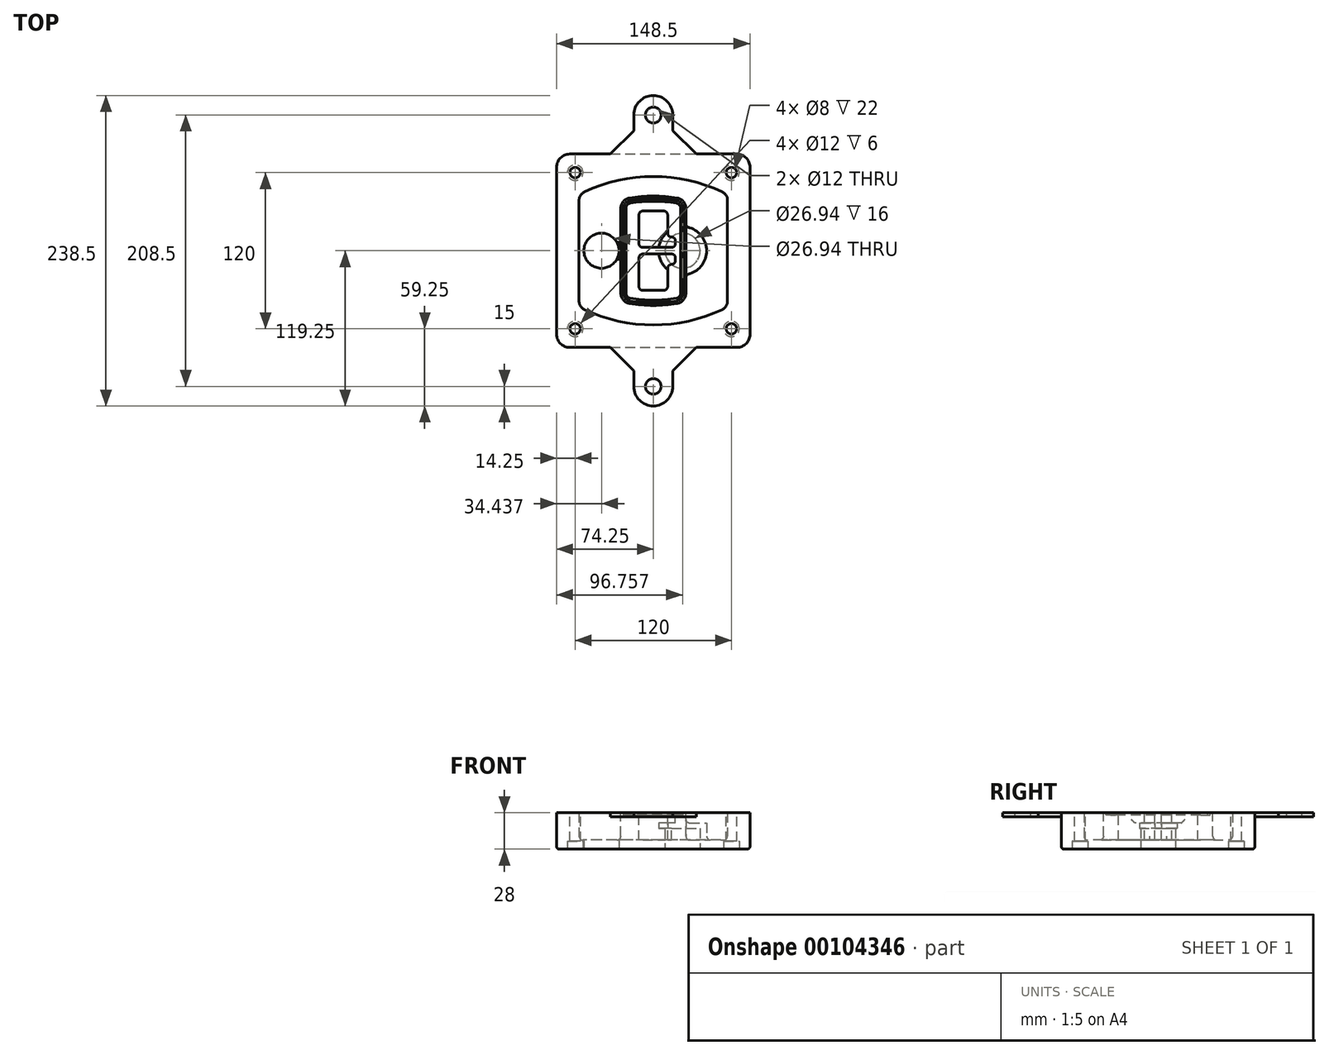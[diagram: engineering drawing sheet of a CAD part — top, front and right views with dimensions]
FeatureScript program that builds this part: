
annotation { "Feature Type Name" : "Feature", "Feature Type Description" : "" }
export const myFeature = defineFeature(function(context is Context, id is Id, definition is map)
    precondition{}
    {
        {
            var Q0;
            Q0=qCreatedBy(makeId("Top.planeOp"),FACE);
            var sketch = newSketch(context, id + "F0", { "sketchPlane" : qUnion([Q0])});
            skPoint(sketch, "E0.rect.middle", {"position": v(0, 0) * mm});
            skLineSegment(sketch, "E1.bottom", {"start": v(-64.25, -74.25) * mm, "end": v(64.25, -74.25) * mm});
            skLineSegment(sketch, "E1.top", {"start": v(-64.25, 74.25) * mm, "end": v(64.25, 74.25) * mm});
            skLineSegment(sketch, "E1.left", {"start": v(-74.25, -64.25) * mm, "end": v(-74.25, 64.25) * mm});
            skLineSegment(sketch, "E1.right", {"start": v(74.25, -64.25) * mm, "end": v(74.25, 64.25) * mm});
            skLineSegment(sketch, "E2", {"start": v(-74.25, 74.25) * mm, "end": v(74.25, -74.25) * mm, "construction": true});
            skLineSegment(sketch, "E3", {"start": v(74.25, 74.25) * mm, "end": v(-74.25, -74.25) * mm, "construction": true});
            skCircle(sketch, "E4", {"center": v(-60, 60) * mm, "radius": 4 * mm});
            skCircle(sketch, "E5", {"center": v(60, 60) * mm, "radius": 4 * mm});
            skCircle(sketch, "E6", {"center": v(60, -60) * mm, "radius": 4 * mm});
            skCircle(sketch, "E7", {"center": v(-60, -60) * mm, "radius": 4 * mm});
            skLineSegment(sketch, "E8", {"start": v(-60, 60) * mm, "end": v(60, 60) * mm, "construction": true});
            skLineSegment(sketch, "E9", {"start": v(60, 60) * mm, "end": v(60, -60) * mm, "construction": true});
            skLineSegment(sketch, "E10", {"start": v(60, -60) * mm, "end": v(-60, -60) * mm, "construction": true});
            skLineSegment(sketch, "E11", {"start": v(-60, -60) * mm, "end": v(-60, 60) * mm, "construction": true});
            skLineSegment(sketch, "E12", {"start": v(-60, 38.83) * mm, "end": v(-60, -38.83) * mm});
            skLineSegment(sketch, "E13", {"start": v(60, 38.83) * mm, "end": v(60, -38.83) * mm});
            skArc(sketch, "E14", {"start": v(54.26, 47.88) * mm, "mid": v(0, 60) * mm, "end": v(-54.26, 47.88) * mm});
            skArc(sketch, "E15", {"start": v(-54.26, -47.88) * mm, "mid": v(0, -60) * mm, "end": v(54.26, -47.88) * mm});
            skLineSegment(sketch, "E16", {"start": v(-60, 0) * mm, "end": v(60, 0) * mm, "construction": true});
            skPoint(sketch, "E17.visualSharp", {"position": v(-60, -45) * mm});
            skArc(sketch, "E17.filletArc", {"start": v(-60, -38.83) * mm, "mid": v(-58.44, -44.2) * mm, "end": v(-54.26, -47.88) * mm});
            skPoint(sketch, "E18.visualSharp", {"position": v(-60, 45) * mm});
            skArc(sketch, "E18.filletArc", {"start": v(-54.26, 47.88) * mm, "mid": v(-58.44, 44.2) * mm, "end": v(-60, 38.83) * mm});
            skPoint(sketch, "E19.visualSharp", {"position": v(60, 45) * mm});
            skArc(sketch, "E19.filletArc", {"start": v(60, 38.83) * mm, "mid": v(58.44, 44.2) * mm, "end": v(54.26, 47.88) * mm});
            skPoint(sketch, "E20.visualSharp", {"position": v(60, -45) * mm});
            skArc(sketch, "E20.filletArc", {"start": v(54.26, -47.88) * mm, "mid": v(58.44, -44.2) * mm, "end": v(60, -38.83) * mm});
            skPoint(sketch, "E21.visualSharp", {"position": v(-74.25, 74.25) * mm});
            skArc(sketch, "E21.filletArc", {"start": v(-64.25, 74.25) * mm, "mid": v(-71.32, 71.32) * mm, "end": v(-74.25, 64.25) * mm});
            skPoint(sketch, "E22.visualSharp", {"position": v(74.25, 74.25) * mm});
            skArc(sketch, "E22.filletArc", {"start": v(74.25, 64.25) * mm, "mid": v(71.32, 71.32) * mm, "end": v(64.25, 74.25) * mm});
            skPoint(sketch, "E23.visualSharp", {"position": v(74.25, -74.25) * mm});
            skArc(sketch, "E23.filletArc", {"start": v(64.25, -74.25) * mm, "mid": v(71.32, -71.32) * mm, "end": v(74.25, -64.25) * mm});
            skPoint(sketch, "E24.visualSharp", {"position": v(-74.25, -74.25) * mm});
            skArc(sketch, "E24.filletArc", {"start": v(-74.25, -64.25) * mm, "mid": v(-71.32, -71.32) * mm, "end": v(-64.25, -74.25) * mm});
            skArc(sketch, "E25.0", {"start": v(57, 38.83) * mm, "mid": v(55.9, 42.58) * mm, "end": v(52.98, 45.17) * mm});
            skLineSegment(sketch, "E25.1", {"start": v(57, 38.83) * mm, "end": v(57, -38.83) * mm});
            skArc(sketch, "E25.2", {"start": v(52.98, -45.17) * mm, "mid": v(55.9, -42.58) * mm, "end": v(57, -38.83) * mm});
            skArc(sketch, "E25.3", {"start": v(-52.98, -45.17) * mm, "mid": v(0, -57) * mm, "end": v(52.98, -45.17) * mm});
            skArc(sketch, "E25.4", {"start": v(-57, -38.83) * mm, "mid": v(-55.9, -42.58) * mm, "end": v(-52.98, -45.17) * mm});
            skArc(sketch, "E25.5", {"start": v(52.98, 45.17) * mm, "mid": v(0, 57) * mm, "end": v(-52.98, 45.17) * mm});
            skLineSegment(sketch, "E25.6", {"start": v(-57, 38.83) * mm, "end": v(-57, -38.83) * mm});
            skArc(sketch, "E25.7", {"start": v(-52.98, 45.17) * mm, "mid": v(-55.9, 42.58) * mm, "end": v(-57, 38.83) * mm});
            skArc(sketch, "E26.0", {"start": v(-55.96, 51.5) * mm, "mid": v(-61.82, 46.33) * mm, "end": v(-64, 38.83) * mm});
            skArc(sketch, "E26.1", {"start": v(55.96, 51.5) * mm, "mid": v(0, 64) * mm, "end": v(-55.96, 51.5) * mm});
            skArc(sketch, "E26.2", {"start": v(64, 38.83) * mm, "mid": v(61.82, 46.33) * mm, "end": v(55.96, 51.5) * mm});
            skLineSegment(sketch, "E26.3", {"start": v(64, 38.83) * mm, "end": v(64, -38.83) * mm});
            skArc(sketch, "E26.4", {"start": v(55.96, -51.5) * mm, "mid": v(61.82, -46.33) * mm, "end": v(64, -38.83) * mm});
            skLineSegment(sketch, "E26.5", {"start": v(-64, 38.83) * mm, "end": v(-64, -38.83) * mm});
            skArc(sketch, "E26.6", {"start": v(-55.96, -51.5) * mm, "mid": v(0, -64) * mm, "end": v(55.96, -51.5) * mm});
            skArc(sketch, "E26.7", {"start": v(-64, -38.83) * mm, "mid": v(-61.82, -46.33) * mm, "end": v(-55.96, -51.5) * mm});
            skSolve(sketch);
        }
        {
            var Q0;
            Q0=makeQuery(id+"F0.imprint","IMPRINT",FACE,{"disambiguationData":[TD([[makeQuery(id+"F0.imprint","IMPRINT",EDGE,{"derivedFrom":sQuery(id+"F0.wireOp",EDGE,"E1.bottom")}),1.0]])]});
            var Q1;
            Q1=makeQuery(id+"F0.imprint","IMPRINT",FACE,{"disambiguationData":[TD([[makeQuery(id+"F0.imprint","IMPRINT",EDGE,{"derivedFrom":sQuery(id+"F0.wireOp",EDGE,"E12")}),1.0]])]});
            var Q2;
            Q2=makeQuery(id+"F0.imprint","IMPRINT",FACE,{"disambiguationData":[TD([[makeQuery(id+"F0.imprint","IMPRINT",EDGE,{"derivedFrom":sQuery(id+"F0.wireOp",EDGE,"E25.0")}),1.0]])]});
            var Q3;
            Q3=makeQuery(id+"F0.imprint","IMPRINT",FACE,{"disambiguationData":[TD([[makeQuery(id+"F0.imprint","IMPRINT",EDGE,{"derivedFrom":sQuery(id+"F0.wireOp",EDGE,"E12")}),-1.0]])]});
            extrude(context, id + "F1", {"entities" : qUnion([Q0, Q1, Q2, Q3]), "oppositeDirection" : true, "depth" : 25 * mm});
        }
        {
            var Q0;
            Q0=makeQuery(id+"F0.imprint","IMPRINT",FACE,{"disambiguationData":[TD([[makeQuery(id+"F0.imprint","IMPRINT",EDGE,{"derivedFrom":sQuery(id+"F0.wireOp",EDGE,"E12")}),1.0]])]});
            extrude(context, id + "F2", {"entities" : qUnion([Q0]), "operationType" : NewBodyOperationType.ADD, "depth" : 3 * mm});
        }
        {
            var Q0;
            Q0=makeQuery(id+"F0.imprint","IMPRINT",FACE,{"disambiguationData":[TD([[makeQuery(id+"F0.imprint","IMPRINT",EDGE,{"derivedFrom":sQuery(id+"F0.wireOp",EDGE,"E25.0")}),1.0]])]});
            extrude(context, id + "F3", {"entities" : qUnion([Q0]), "operationType" : NewBodyOperationType.REMOVE, "oppositeDirection" : true, "depth" : 18 * mm});
        }
        {
            var Q0;
            Q0=makeQuery(id+"F2.opExtrude","CAP_FACE",FACE,{"disambiguationData":[OSD([sQuery(id+"F0.wireOp",EDGE,"E12"),sQuery(id+"F0.wireOp",EDGE,"E13"),sQuery(id+"F0.wireOp",EDGE,"E14"),sQuery(id+"F0.wireOp",EDGE,"E15"),sQuery(id+"F0.wireOp",EDGE,"E17.filletArc"),sQuery(id+"F0.wireOp",EDGE,"E18.filletArc"),sQuery(id+"F0.wireOp",EDGE,"E19.filletArc"),sQuery(id+"F0.wireOp",EDGE,"E20.filletArc"),sQuery(id+"F0.wireOp",EDGE,"E25.0"),sQuery(id+"F0.wireOp",EDGE,"E25.1"),sQuery(id+"F0.wireOp",EDGE,"E25.2"),sQuery(id+"F0.wireOp",EDGE,"E25.3"),sQuery(id+"F0.wireOp",EDGE,"E25.4"),sQuery(id+"F0.wireOp",EDGE,"E25.5"),sQuery(id+"F0.wireOp",EDGE,"E25.6"),sQuery(id+"F0.wireOp",EDGE,"E25.7")])],"isStart":false});
            var sketch = newSketch(context, id + "F4", { "sketchPlane" : qUnion([Q0])});
            skArc(sketch, "E27.0", {"start": v(-18.34, -40.45) * mm, "mid": v(0, -42) * mm, "end": v(18.34, -40.45) * mm});
            skArc(sketch, "E28.0", {"start": v(18.34, 40.45) * mm, "mid": v(0, 42) * mm, "end": v(-18.34, 40.45) * mm});
            skLineSegment(sketch, "E29", {"start": v(-25, 32.57) * mm, "end": v(-25, -32.57) * mm});
            skLineSegment(sketch, "E30", {"start": v(25, 32.57) * mm, "end": v(25, -32.57) * mm});
            skLineSegment(sketch, "E31", {"start": v(-25, 39.1) * mm, "end": v(25, 39.1) * mm, "construction": true});
            skLineSegment(sketch, "E32", {"start": v(-25, -39.1) * mm, "end": v(25, -39.1) * mm, "construction": true});
            skPoint(sketch, "E33.visualSharp", {"position": v(-25, 39.1) * mm});
            skArc(sketch, "E33.filletArc", {"start": v(-18.34, 40.45) * mm, "mid": v(-23.11, 37.73) * mm, "end": v(-25, 32.57) * mm});
            skPoint(sketch, "E34.visualSharp", {"position": v(25, 39.1) * mm});
            skArc(sketch, "E34.filletArc", {"start": v(25, 32.57) * mm, "mid": v(23.11, 37.73) * mm, "end": v(18.34, 40.45) * mm});
            skPoint(sketch, "E35.visualSharp", {"position": v(25, -39.1) * mm});
            skArc(sketch, "E35.filletArc", {"start": v(18.34, -40.45) * mm, "mid": v(23.11, -37.73) * mm, "end": v(25, -32.57) * mm});
            skPoint(sketch, "E36.visualSharp", {"position": v(-25, -39.1) * mm});
            skArc(sketch, "E36.filletArc", {"start": v(-25, -32.57) * mm, "mid": v(-23.11, -37.73) * mm, "end": v(-18.34, -40.45) * mm});
            skArc(sketch, "E37.0", {"start": v(52.98, 45.17) * mm, "mid": v(0, 57) * mm, "end": v(-52.98, 45.17) * mm});
            skArc(sketch, "E37.1", {"start": v(-52.98, 45.17) * mm, "mid": v(-55.9, 42.58) * mm, "end": v(-57, 38.83) * mm});
            skLineSegment(sketch, "E37.2", {"start": v(-57, 38.83) * mm, "end": v(-57, -38.83) * mm});
            skArc(sketch, "E37.3", {"start": v(-57, -38.83) * mm, "mid": v(-55.9, -42.58) * mm, "end": v(-52.98, -45.17) * mm});
            skArc(sketch, "E37.4", {"start": v(-52.98, -45.17) * mm, "mid": v(0, -57) * mm, "end": v(52.98, -45.17) * mm});
            skArc(sketch, "E37.5", {"start": v(52.98, -45.17) * mm, "mid": v(55.9, -42.58) * mm, "end": v(57, -38.83) * mm});
            skLineSegment(sketch, "E37.6", {"start": v(57, 38.83) * mm, "end": v(57, -38.83) * mm});
            skArc(sketch, "E37.7", {"start": v(57, 38.83) * mm, "mid": v(55.9, 42.58) * mm, "end": v(52.98, 45.17) * mm});
            skLineSegment(sketch, "E38.0", {"start": v(23, 32.57) * mm, "end": v(23, -32.57) * mm});
            skArc(sketch, "E38.1", {"start": v(18, -38.48) * mm, "mid": v(21.58, -36.44) * mm, "end": v(23, -32.57) * mm});
            skArc(sketch, "E38.2", {"start": v(-18, -38.48) * mm, "mid": v(0, -40) * mm, "end": v(18, -38.48) * mm});
            skArc(sketch, "E38.3", {"start": v(-23, -32.57) * mm, "mid": v(-21.58, -36.44) * mm, "end": v(-18, -38.48) * mm});
            skLineSegment(sketch, "E38.4", {"start": v(-23, 32.57) * mm, "end": v(-23, -32.57) * mm});
            skArc(sketch, "E38.5", {"start": v(23, 32.57) * mm, "mid": v(21.58, 36.44) * mm, "end": v(18, 38.48) * mm});
            skArc(sketch, "E38.6", {"start": v(-18, 38.48) * mm, "mid": v(-21.58, 36.44) * mm, "end": v(-23, 32.57) * mm});
            skArc(sketch, "E38.7", {"start": v(18, 38.48) * mm, "mid": v(0, 40) * mm, "end": v(-18, 38.48) * mm});
            skArc(sketch, "E39.0", {"start": v(21, 32.57) * mm, "mid": v(20.06, 35.15) * mm, "end": v(17.67, 36.5) * mm});
            skLineSegment(sketch, "E39.1", {"start": v(21, 32.57) * mm, "end": v(21, -32.57) * mm});
            skArc(sketch, "E39.2", {"start": v(17.67, -36.5) * mm, "mid": v(20.06, -35.15) * mm, "end": v(21, -32.57) * mm});
            skArc(sketch, "E39.3", {"start": v(-17.67, -36.5) * mm, "mid": v(0, -38) * mm, "end": v(17.67, -36.5) * mm});
            skArc(sketch, "E39.4", {"start": v(-21, -32.57) * mm, "mid": v(-20.06, -35.15) * mm, "end": v(-17.67, -36.5) * mm});
            skArc(sketch, "E39.5", {"start": v(17.67, 36.5) * mm, "mid": v(0, 38) * mm, "end": v(-17.67, 36.5) * mm});
            skLineSegment(sketch, "E39.6", {"start": v(-21, 32.57) * mm, "end": v(-21, -32.57) * mm});
            skArc(sketch, "E39.7", {"start": v(-17.67, 36.5) * mm, "mid": v(-20.06, 35.15) * mm, "end": v(-21, 32.57) * mm});
            skLineSegment(sketch, "E40", {"start": v(-25, 0) * mm, "end": v(25, 0) * mm, "construction": true});
            skLineSegment(sketch, "E41", {"start": v(-11, 5.5) * mm, "end": v(-11, 27.5) * mm});
            skLineSegment(sketch, "E42", {"start": v(-8, 30.5) * mm, "end": v(8, 30.5) * mm});
            skLineSegment(sketch, "E43", {"start": v(11, 27.5) * mm, "end": v(11, 13.5) * mm});
            skLineSegment(sketch, "E44", {"start": v(14, 10.5) * mm, "end": v(14, 10.5) * mm});
            skLineSegment(sketch, "E45", {"start": v(17, 7.5) * mm, "end": v(17, 5.5) * mm});
            skLineSegment(sketch, "E46", {"start": v(14, 2.5) * mm, "end": v(-8, 2.5) * mm});
            skPoint(sketch, "E47.visualSharp", {"position": v(-11, 30.5) * mm});
            skArc(sketch, "E47.filletArc", {"start": v(-8, 30.5) * mm, "mid": v(-10.12, 29.62) * mm, "end": v(-11, 27.5) * mm});
            skPoint(sketch, "E48.visualSharp", {"position": v(11, 30.5) * mm});
            skArc(sketch, "E48.filletArc", {"start": v(11, 27.5) * mm, "mid": v(10.12, 29.62) * mm, "end": v(8, 30.5) * mm});
            skPoint(sketch, "E49.visualSharp", {"position": v(11, 10.5) * mm});
            skArc(sketch, "E49.filletArc", {"start": v(11, 13.5) * mm, "mid": v(11.88, 11.38) * mm, "end": v(14, 10.5) * mm});
            skPoint(sketch, "E50.visualSharp", {"position": v(17, 10.5) * mm});
            skArc(sketch, "E50.filletArc", {"start": v(17, 7.5) * mm, "mid": v(16.12, 9.62) * mm, "end": v(14, 10.5) * mm});
            skPoint(sketch, "E51.visualSharp", {"position": v(17, 2.5) * mm});
            skArc(sketch, "E51.filletArc", {"start": v(14, 2.5) * mm, "mid": v(16.12, 3.38) * mm, "end": v(17, 5.5) * mm});
            skPoint(sketch, "E52.visualSharp", {"position": v(-11, 2.5) * mm});
            skArc(sketch, "E52.filletArc", {"start": v(-11, 5.5) * mm, "mid": v(-10.12, 3.38) * mm, "end": v(-8, 2.5) * mm});
            skLineSegment(sketch, "E53.0.MirrorCS", {"start": v(14, -2.5) * mm, "end": v(-8, -2.5) * mm});
            skArc(sketch, "E54.0.MirrorCS", {"start": v(-11, -5.5) * mm, "mid": v(-10.12, -3.38) * mm, "end": v(-8, -2.5) * mm});
            skLineSegment(sketch, "E55.0.MirrorCS", {"start": v(-11, -5.5) * mm, "end": v(-11, -27.5) * mm});
            skArc(sketch, "E56.0.MirrorCS", {"start": v(-8, -30.5) * mm, "mid": v(-10.12, -29.62) * mm, "end": v(-11, -27.5) * mm});
            skLineSegment(sketch, "E57.0.MirrorCS", {"start": v(-8, -30.5) * mm, "end": v(8, -30.5) * mm});
            skArc(sketch, "E58.0.MirrorCS", {"start": v(11, -27.5) * mm, "mid": v(10.12, -29.62) * mm, "end": v(8, -30.5) * mm});
            skLineSegment(sketch, "E59.0.MirrorCS", {"start": v(11, -27.5) * mm, "end": v(11, -13.5) * mm});
            skArc(sketch, "E60.0.MirrorCS", {"start": v(11, -13.5) * mm, "mid": v(11.88, -11.38) * mm, "end": v(14, -10.5) * mm});
            skArc(sketch, "E61.0.MirrorCS", {"start": v(17, -7.5) * mm, "mid": v(16.12, -9.62) * mm, "end": v(14, -10.5) * mm});
            skLineSegment(sketch, "E62.0.MirrorCS", {"start": v(17, -7.5) * mm, "end": v(17, -5.5) * mm});
            skArc(sketch, "E63.0.MirrorCS", {"start": v(14, -2.5) * mm, "mid": v(16.12, -3.38) * mm, "end": v(17, -5.5) * mm});
            skSolve(sketch);
        }
        {
            var Q0;
            Q0=makeQuery(id+"F4.imprint","IMPRINT",FACE,{"disambiguationData":[TD([[makeQuery(id+"F4.imprint","IMPRINT",EDGE,{"derivedFrom":sQuery(id+"F4.wireOp",EDGE,"E27.0")}),1.0]])]});
            var Q1;
            Q1=makeQuery(id+"F4.imprint","IMPRINT",FACE,{"disambiguationData":[TD([[makeQuery(id+"F4.imprint","IMPRINT",EDGE,{"derivedFrom":sQuery(id+"F4.wireOp",EDGE,"E38.0")}),-1.0]])]});
            var Q2;
            Q2=makeQuery(id+"F4.imprint","IMPRINT",FACE,{"disambiguationData":[TD([[makeQuery(id+"F4.imprint","IMPRINT",EDGE,{"derivedFrom":sQuery(id+"F4.wireOp",EDGE,"E39.0")}),1.0]])]});
            extrude(context, id + "F5", {"entities" : qUnion([Q0, Q1, Q2]), "operationType" : NewBodyOperationType.ADD, "endBound" : BoundingType.UP_TO_NEXT, "oppositeDirection" : true, "depth" : 25 * mm});
        }
        {
            var Q0;
            Q0=makeQuery(id+"F4.imprint","IMPRINT",FACE,{"disambiguationData":[TD([[makeQuery(id+"F4.imprint","IMPRINT",EDGE,{"derivedFrom":sQuery(id+"F4.wireOp",EDGE,"E38.0")}),-1.0]])]});
            extrude(context, id + "F6", {"entities" : qUnion([Q0]), "operationType" : NewBodyOperationType.REMOVE, "oppositeDirection" : true, "depth" : 2 * mm});
        }
        {
            var Q0;
            Q0=makeQuery(id+"F1.opExtrude","CAP_FACE",FACE,{"disambiguationData":[OSD([sQuery(id+"F0.wireOp",EDGE,"E1.bottom"),sQuery(id+"F0.wireOp",EDGE,"E1.top"),sQuery(id+"F0.wireOp",EDGE,"E1.left"),sQuery(id+"F0.wireOp",EDGE,"E1.right"),sQuery(id+"F0.wireOp",EDGE,"E4"),sQuery(id+"F0.wireOp",EDGE,"E5"),sQuery(id+"F0.wireOp",EDGE,"E6"),sQuery(id+"F0.wireOp",EDGE,"E7"),sQuery(id+"F0.wireOp",EDGE,"E21.filletArc"),sQuery(id+"F0.wireOp",EDGE,"E22.filletArc"),sQuery(id+"F0.wireOp",EDGE,"E23.filletArc"),sQuery(id+"F0.wireOp",EDGE,"E24.filletArc")])],"isStart":false});
            var sketch = newSketch(context, id + "F7", { "sketchPlane" : qUnion([Q0])});
            skCircle(sketch, "E64", {"center": v(22.5, 0) * mm, "radius": 13.47 * mm});
            skCircle(sketch, "E65", {"center": v(-39.81, 0) * mm, "radius": 13.47 * mm});
            skLineSegment(sketch, "E66", {"start": v(74.25, 0) * mm, "end": v(-74.25, 0) * mm});
            skCircle(sketch, "E67", {"center": v(22.5, 0) * mm, "radius": 18.47 * mm});
            skCircle(sketch, "E68", {"center": v(60, -60) * mm, "radius": 6 * mm});
            skCircle(sketch, "E69", {"center": v(-60, -60) * mm, "radius": 6 * mm});
            skCircle(sketch, "E70", {"center": v(-60, 60) * mm, "radius": 6 * mm});
            skCircle(sketch, "E71", {"center": v(60, 60) * mm, "radius": 6 * mm});
            skSolve(sketch);
        }
        {
            var Q0;
            {var subQ1=sQuery(id+"F7.wireOp",EDGE,"E66");var subQ4=sQuery(id+"F7.wireOp",EDGE,"E64");var subQ6=makeQuery(id+"F7.imprint","INTERSECT",VERTEX,{"disambiguationData":[OD(0.0)],"derivedFrom":[subQ4,subQ1]});Q0=makeQuery(id+"F7.imprint","IMPRINT",FACE,{"disambiguationData":[TD([[makeQuery(id+"F7.imprint","IMPRINT",EDGE,{"disambiguationData":[TD([[subQ6,-1.0]])],"derivedFrom":subQ4}),-1.0]])]});}
            var Q1;
            {var subQ0=sQuery(id+"F7.wireOp",EDGE,"E66");var subQ1=sQuery(id+"F7.wireOp",EDGE,"E64");var subQ3=makeQuery(id+"F7.imprint","INTERSECT",VERTEX,{"disambiguationData":[OD(0.0)],"derivedFrom":[subQ1,subQ0]});Q1=makeQuery(id+"F7.imprint","IMPRINT",FACE,{"disambiguationData":[TD([[makeQuery(id+"F7.imprint","IMPRINT",EDGE,{"disambiguationData":[TD([[subQ3,-1.0]])],"derivedFrom":subQ1}),1.0]])]});}
            var Q2;
            {var subQ0=sQuery(id+"F7.wireOp",EDGE,"E66");var subQ1=sQuery(id+"F7.wireOp",EDGE,"E64");var subQ3=makeQuery(id+"F7.imprint","INTERSECT",VERTEX,{"disambiguationData":[OD(0.0)],"derivedFrom":[subQ1,subQ0]});Q2=makeQuery(id+"F7.imprint","IMPRINT",FACE,{"disambiguationData":[TD([[makeQuery(id+"F7.imprint","IMPRINT",EDGE,{"disambiguationData":[TD([[subQ3,1.0]])],"derivedFrom":subQ1}),1.0]])]});}
            var Q3;
            {var subQ1=sQuery(id+"F7.wireOp",EDGE,"E66");var subQ4=sQuery(id+"F7.wireOp",EDGE,"E64");var subQ6=makeQuery(id+"F7.imprint","INTERSECT",VERTEX,{"disambiguationData":[OD(0.0)],"derivedFrom":[subQ4,subQ1]});Q3=makeQuery(id+"F7.imprint","IMPRINT",FACE,{"disambiguationData":[TD([[makeQuery(id+"F7.imprint","IMPRINT",EDGE,{"disambiguationData":[TD([[subQ6,1.0]])],"derivedFrom":subQ4}),-1.0]])]});}
            extrude(context, id + "F8", {"entities" : qUnion([Q0, Q1, Q2, Q3]), "operationType" : NewBodyOperationType.ADD, "oppositeDirection" : true, "depth" : 20 * mm});
        }
        {
            var Q0;
            {var subQ0=sQuery(id+"F7.wireOp",EDGE,"E66");var subQ1=sQuery(id+"F7.wireOp",EDGE,"E64");var subQ3=makeQuery(id+"F7.imprint","INTERSECT",VERTEX,{"disambiguationData":[OD(0.0)],"derivedFrom":[subQ1,subQ0]});Q0=makeQuery(id+"F7.imprint","IMPRINT",FACE,{"disambiguationData":[TD([[makeQuery(id+"F7.imprint","IMPRINT",EDGE,{"disambiguationData":[TD([[subQ3,-1.0]])],"derivedFrom":subQ1}),1.0]])]});}
            var Q1;
            {var subQ0=sQuery(id+"F7.wireOp",EDGE,"E66");var subQ1=sQuery(id+"F7.wireOp",EDGE,"E64");var subQ3=makeQuery(id+"F7.imprint","INTERSECT",VERTEX,{"disambiguationData":[OD(0.0)],"derivedFrom":[subQ1,subQ0]});Q1=makeQuery(id+"F7.imprint","IMPRINT",FACE,{"disambiguationData":[TD([[makeQuery(id+"F7.imprint","IMPRINT",EDGE,{"disambiguationData":[TD([[subQ3,1.0]])],"derivedFrom":subQ1}),1.0]])]});}
            extrude(context, id + "F9", {"entities" : qUnion([Q0, Q1]), "operationType" : NewBodyOperationType.REMOVE, "oppositeDirection" : true, "depth" : 16 * mm});
        }
        {
            var Q0;
            {var subQ0=sQuery(id+"F7.wireOp",EDGE,"E66");var subQ1=sQuery(id+"F7.wireOp",EDGE,"E65");var subQ3=makeQuery(id+"F7.imprint","INTERSECT",VERTEX,{"disambiguationData":[OD(0.0)],"derivedFrom":[subQ1,subQ0]});Q0=makeQuery(id+"F7.imprint","IMPRINT",FACE,{"disambiguationData":[TD([[makeQuery(id+"F7.imprint","IMPRINT",EDGE,{"disambiguationData":[TD([[subQ3,-1.0]])],"derivedFrom":subQ1}),1.0]])]});}
            var Q1;
            {var subQ0=sQuery(id+"F7.wireOp",EDGE,"E66");var subQ1=sQuery(id+"F7.wireOp",EDGE,"E65");var subQ3=makeQuery(id+"F7.imprint","INTERSECT",VERTEX,{"disambiguationData":[OD(0.0)],"derivedFrom":[subQ1,subQ0]});Q1=makeQuery(id+"F7.imprint","IMPRINT",FACE,{"disambiguationData":[TD([[makeQuery(id+"F7.imprint","IMPRINT",EDGE,{"disambiguationData":[TD([[subQ3,1.0]])],"derivedFrom":subQ1}),1.0]])]});}
            extrude(context, id + "F10", {"entities" : qUnion([Q0, Q1]), "operationType" : NewBodyOperationType.REMOVE, "oppositeDirection" : true, "depth" : 25 * mm});
        }
        {
            var Q0;
            Q0=makeQuery(id+"F7.imprint","IMPRINT",FACE,{"disambiguationData":[TD([[makeQuery(id+"F7.imprint","IMPRINT",EDGE,{"derivedFrom":sQuery(id+"F7.wireOp",EDGE,"E68")}),1.0]])]});
            var Q1;
            Q1=makeQuery(id+"F7.imprint","IMPRINT",FACE,{"disambiguationData":[TD([[makeQuery(id+"F7.imprint","IMPRINT",EDGE,{"derivedFrom":makeQuery(id+"F1.opExtrude","CAP_EDGE",EDGE,{"disambiguationData":[OSD([sQuery(id+"F0.wireOp",EDGE,"E5")])],"isStart":false})}),-1.0]])]});
            var Q2;
            Q2=makeQuery(id+"F7.imprint","IMPRINT",FACE,{"disambiguationData":[TD([[makeQuery(id+"F7.imprint","IMPRINT",EDGE,{"derivedFrom":sQuery(id+"F7.wireOp",EDGE,"E69")}),1.0]])]});
            var Q3;
            Q3=makeQuery(id+"F7.imprint","IMPRINT",FACE,{"disambiguationData":[TD([[makeQuery(id+"F7.imprint","IMPRINT",EDGE,{"derivedFrom":makeQuery(id+"F1.opExtrude","CAP_EDGE",EDGE,{"disambiguationData":[OSD([sQuery(id+"F0.wireOp",EDGE,"E4")])],"isStart":false})}),-1.0]])]});
            var Q4;
            Q4=makeQuery(id+"F7.imprint","IMPRINT",FACE,{"disambiguationData":[TD([[makeQuery(id+"F7.imprint","IMPRINT",EDGE,{"derivedFrom":sQuery(id+"F7.wireOp",EDGE,"E70")}),1.0]])]});
            var Q5;
            Q5=makeQuery(id+"F7.imprint","IMPRINT",FACE,{"disambiguationData":[TD([[makeQuery(id+"F7.imprint","IMPRINT",EDGE,{"derivedFrom":makeQuery(id+"F1.opExtrude","CAP_EDGE",EDGE,{"disambiguationData":[OSD([sQuery(id+"F0.wireOp",EDGE,"E7")])],"isStart":false})}),-1.0]])]});
            var Q6;
            Q6=makeQuery(id+"F7.imprint","IMPRINT",FACE,{"disambiguationData":[TD([[makeQuery(id+"F7.imprint","IMPRINT",EDGE,{"derivedFrom":sQuery(id+"F7.wireOp",EDGE,"E71")}),1.0]])]});
            var Q7;
            Q7=makeQuery(id+"F7.imprint","IMPRINT",FACE,{"disambiguationData":[TD([[makeQuery(id+"F7.imprint","IMPRINT",EDGE,{"derivedFrom":makeQuery(id+"F1.opExtrude","CAP_EDGE",EDGE,{"disambiguationData":[OSD([sQuery(id+"F0.wireOp",EDGE,"E6")])],"isStart":false})}),-1.0]])]});
            extrude(context, id + "F11", {"entities" : qUnion([Q0, Q1, Q2, Q3, Q4, Q5, Q6, Q7]), "operationType" : NewBodyOperationType.REMOVE, "oppositeDirection" : true, "depth" : 6 * mm});
        }
        {
            var Q0;
            Q0=makeQuery(id+"F9.boolean.opBoolean","COPY",FACE,{"derivedFrom":makeQuery(id+"F9.opExtrude","CAP_FACE",FACE,{"disambiguationData":[OSD([sQuery(id+"F7.wireOp",EDGE,"E64")])],"isStart":false})});
            var sketch = newSketch(context, id + "F12", { "sketchPlane" : qUnion([Q0])});
            skArc(sketch, "E72.0", {"start": v(11, 14.45) * mm, "mid": v(6.45, 9.13) * mm, "end": v(4.2, 2.5) * mm});
            skArc(sketch, "E72.1", {"start": v(4.2, -2.5) * mm, "mid": v(6.45, -9.13) * mm, "end": v(11, -14.45) * mm});
            skLineSegment(sketch, "E73", {"start": v(4.2, -2.5) * mm, "end": v(14, -2.5) * mm});
            skLineSegment(sketch, "E74.0", {"start": v(14, 2.5) * mm, "end": v(4.2, 2.5) * mm});
            skArc(sketch, "E74.1", {"start": v(14, 2.5) * mm, "mid": v(16.12, 3.38) * mm, "end": v(17, 5.5) * mm});
            skLineSegment(sketch, "E74.2", {"start": v(17, 7.5) * mm, "end": v(17, 5.5) * mm});
            skArc(sketch, "E74.3", {"start": v(17, 7.5) * mm, "mid": v(16.12, 9.62) * mm, "end": v(14, 10.5) * mm});
            skArc(sketch, "E74.4", {"start": v(11, 13.5) * mm, "mid": v(11.88, 11.38) * mm, "end": v(14, 10.5) * mm});
            skLineSegment(sketch, "E74.5", {"start": v(11, 14.45) * mm, "end": v(11, 13.5) * mm});
            skLineSegment(sketch, "E74.7", {"start": v(14, -2.5) * mm, "end": v(4.2, -2.5) * mm});
            skArc(sketch, "E74.8", {"start": v(14, -2.5) * mm, "mid": v(16.12, -3.38) * mm, "end": v(17, -5.5) * mm});
            skLineSegment(sketch, "E74.9", {"start": v(17, -7.5) * mm, "end": v(17, -5.5) * mm});
            skArc(sketch, "E74.10", {"start": v(17, -7.5) * mm, "mid": v(16.12, -9.62) * mm, "end": v(14, -10.5) * mm});
            skArc(sketch, "E74.11", {"start": v(11, -13.5) * mm, "mid": v(11.88, -11.38) * mm, "end": v(14, -10.5) * mm});
            skLineSegment(sketch, "E74.12", {"start": v(11, -14.45) * mm, "end": v(11, -13.5) * mm});
            skPoint(sketch, "E75.orphan", {"position": v(11, -27.5) * mm});
            skPoint(sketch, "E76.orphan", {"position": v(-8, -2.5) * mm});
            skPoint(sketch, "E77.orphan", {"position": v(-8, 2.5) * mm});
            skPoint(sketch, "E78.orphan", {"position": v(11, 27.5) * mm});
            skSolve(sketch);
        }
        {
            var Q0;
            {var subQ7=sQuery(id+"F12.wireOp",EDGE,"E72.0");var subQ14=sQuery(id+"F12.wireOp",EDGE,"E72.1");var subQ16=sQuery(id+"F12.wireOp",EDGE,"E74.1");var subQ18=sQuery(id+"F12.wireOp",EDGE,"E74.8");Q0=qUnion([makeQuery(id+"F12.imprint","IMPRINT",FACE,{"disambiguationData":[TD([[makeQuery(id+"F12.imprint","IMPRINT",EDGE,{"derivedFrom":subQ7}),1.0]])]}),makeQuery(id+"F12.imprint","IMPRINT",FACE,{"disambiguationData":[TD([[makeQuery(id+"F12.imprint","IMPRINT",EDGE,{"derivedFrom":subQ14}),1.0]])]}),makeQuery(id+"F12.imprint","IMPRINT",FACE,{"disambiguationData":[TD([[makeQuery(id+"F12.imprint","IMPRINT",EDGE,{"derivedFrom":subQ16}),1.0]])]}),makeQuery(id+"F12.imprint","IMPRINT",FACE,{"disambiguationData":[TD([[makeQuery(id+"F12.imprint","IMPRINT",EDGE,{"derivedFrom":subQ18}),-1.0]])]})]);}
            var Q1;
            Q1=makeQuery(id+"F5.boolean.opBoolean","SPLIT",FACE,{"disambiguationData":[TD([makeQuery(id+"F5.opExtrude","SWEPT_FACE",FACE,{"disambiguationData":[OSD([sQuery(id+"F4.wireOp",EDGE,"E41")])]})])],"derivedFrom":makeQuery(id+"F3.boolean.opBoolean","COPY",FACE,{"derivedFrom":makeQuery(id+"F3.opExtrude","CAP_FACE",FACE,{"disambiguationData":[OSD([sQuery(id+"F0.wireOp",EDGE,"E25.0"),sQuery(id+"F0.wireOp",EDGE,"E25.1"),sQuery(id+"F0.wireOp",EDGE,"E25.2"),sQuery(id+"F0.wireOp",EDGE,"E25.3"),sQuery(id+"F0.wireOp",EDGE,"E25.4"),sQuery(id+"F0.wireOp",EDGE,"E25.5"),sQuery(id+"F0.wireOp",EDGE,"E25.6"),sQuery(id+"F0.wireOp",EDGE,"E25.7")])],"isStart":false})})});
            extrude(context, id + "F13", {"entities" : qUnion([Q0]), "operationType" : NewBodyOperationType.REMOVE, "endBound" : BoundingType.UP_TO_SURFACE, "endBoundEntityFace" : qUnion([Q1]), "depth" : 25 * mm});
        }
        {
            var Q0;
            Q0=makeQuery(id+"F3.boolean.opBoolean","COPY",EDGE,{"derivedFrom":makeQuery(id+"F3.opExtrude","CAP_EDGE",EDGE,{"disambiguationData":[OSD([sQuery(id+"F0.wireOp",EDGE,"E25.6")])],"isStart":false})});
            var Q1;
            Q1=makeQuery(id+"F8.boolean.opBoolean","INTERSECT",EDGE,{"derivedFrom":[makeQuery(id+"F5.opExtrude","SWEPT_FACE",FACE,{"disambiguationData":[OSD([sQuery(id+"F4.wireOp",EDGE,"E30")])]}),makeQuery(id+"F8.opExtrude","CAP_FACE",FACE,{"disambiguationData":[OSD([sQuery(id+"F7.wireOp",EDGE,"E67")])],"isStart":false})]});
            var Q2;
            Q2=makeQuery(id+"F8.boolean.opBoolean","INTERSECT",EDGE,{"disambiguationData":[OD(1.0)],"derivedFrom":[makeQuery(id+"F5.opExtrude","SWEPT_FACE",FACE,{"disambiguationData":[OSD([sQuery(id+"F4.wireOp",EDGE,"E30")])]}),makeQuery(id+"F8.opExtrude","SWEPT_FACE",FACE,{"disambiguationData":[OSD([sQuery(id+"F7.wireOp",EDGE,"E67")])]})]});
            var Q3;
            {var subQ0=sQuery(id+"F4.wireOp",EDGE,"E30");Q3=makeQuery(id+"F8.boolean.opBoolean","SPLIT",EDGE,{"disambiguationData":[TD([makeQuery(id+"F5.opExtrude","SWEPT_FACE",FACE,{"disambiguationData":[OSD([sQuery(id+"F4.wireOp",EDGE,"E35.filletArc")])]})])],"derivedFrom":makeQuery(id+"F5.opExtrude","CAP_EDGE",EDGE,{"disambiguationData":[OSD([subQ0])],"isStart":false})});}
            var Q4;
            {var subQ0=sQuery(id+"F0.wireOp",EDGE,"E25.7");var subQ1=sQuery(id+"F0.wireOp",EDGE,"E25.1");var subQ2=sQuery(id+"F0.wireOp",EDGE,"E25.6");var subQ3=sQuery(id+"F0.wireOp",EDGE,"E25.5");var subQ4=sQuery(id+"F0.wireOp",EDGE,"E25.4");var subQ5=sQuery(id+"F0.wireOp",EDGE,"E25.0");var subQ6=sQuery(id+"F0.wireOp",EDGE,"E25.2");var subQ7=sQuery(id+"F0.wireOp",EDGE,"E25.3");Q4=makeQuery(id+"F8.boolean.opBoolean","INTERSECT",EDGE,{"derivedFrom":[makeQuery(id+"F5.boolean.opBoolean","SPLIT",FACE,{"disambiguationData":[TD([makeQuery(id+"F2.opExtrude","SWEPT_FACE",FACE,{"disambiguationData":[OSD([subQ5])]})])],"derivedFrom":makeQuery(id+"F3.boolean.opBoolean","COPY",FACE,{"derivedFrom":makeQuery(id+"F3.opExtrude","CAP_FACE",FACE,{"disambiguationData":[OSD([subQ5,subQ1,subQ6,subQ7,subQ4,subQ3,subQ2,subQ0])],"isStart":false})})}),makeQuery(id+"F8.opExtrude","SWEPT_FACE",FACE,{"disambiguationData":[OSD([sQuery(id+"F7.wireOp",EDGE,"E67")])]})]});}
            var Q5;
            Q5=makeQuery(id+"F8.boolean.opBoolean","INTERSECT",EDGE,{"disambiguationData":[OD(0.0)],"derivedFrom":[makeQuery(id+"F5.opExtrude","SWEPT_FACE",FACE,{"disambiguationData":[OSD([sQuery(id+"F4.wireOp",EDGE,"E30")])]}),makeQuery(id+"F8.opExtrude","SWEPT_FACE",FACE,{"disambiguationData":[OSD([sQuery(id+"F7.wireOp",EDGE,"E67")])]})]});
            fillet(context, id + "F14", {"entities" : qUnion([Q0, Q1, Q2, Q3, Q4, Q5]), "radius" : 3 * mm, "tangentPropagation" : true, "allowEdgeOverflow" : false});
        }
        {
            var Q0;
            Q0=makeQuery(id+"F1.opExtrude","CAP_EDGE",EDGE,{"disambiguationData":[OSD([sQuery(id+"F0.wireOp",EDGE,"E1.bottom")])],"isStart":false});
            fillet(context, id + "F15", {"entities" : qUnion([Q0]), "radius" : 2 * mm, "tangentPropagation" : true, "allowEdgeOverflow" : false});
        }
        {
            var Q0;
            {var subQ0=sQuery(id+"F0.wireOp",EDGE,"E22.filletArc");var subQ1=sQuery(id+"F0.wireOp",EDGE,"E7");var subQ2=sQuery(id+"F0.wireOp",EDGE,"E6");var subQ3=sQuery(id+"F0.wireOp",EDGE,"E5");var subQ4=sQuery(id+"F0.wireOp",EDGE,"E4");var subQ5=sQuery(id+"F0.wireOp",EDGE,"E1.bottom");var subQ6=sQuery(id+"F0.wireOp",EDGE,"E21.filletArc");var subQ7=sQuery(id+"F0.wireOp",EDGE,"E1.top");var subQ8=sQuery(id+"F0.wireOp",EDGE,"E1.left");var subQ9=sQuery(id+"F0.wireOp",EDGE,"E1.right");var subQ10=sQuery(id+"F0.wireOp",EDGE,"E23.filletArc");var subQ11=sQuery(id+"F0.wireOp",EDGE,"E24.filletArc");Q0=makeQuery(id+"F2.boolean.opBoolean","SPLIT",FACE,{"disambiguationData":[TD([makeQuery(id+"F1.opExtrude","SWEPT_FACE",FACE,{"disambiguationData":[OSD([subQ5])]})])],"derivedFrom":makeQuery(id+"F1.opExtrude","CAP_FACE",FACE,{"disambiguationData":[OSD([subQ5,subQ7,subQ8,subQ9,subQ4,subQ3,subQ2,subQ1,subQ6,subQ0,subQ10,subQ11])],"isStart":true})});}
            var sketch = newSketch(context, id + "F16", { "sketchPlane" : qUnion([Q0])});
            skLineSegment(sketch, "E79", {"start": v(0, 74.25) * mm, "end": v(0, 104.25) * mm, "construction": true});
            skCircle(sketch, "E80", {"center": v(0, 104.25) * mm, "radius": 6 * mm});
            skLineSegment(sketch, "E81", {"start": v(-33, 74.25) * mm, "end": v(-15, 92.25) * mm});
            skLineSegment(sketch, "E82", {"start": v(-15, 92.25) * mm, "end": v(-15, 104.25) * mm});
            skArc(sketch, "E83", {"start": v(15, 104.25) * mm, "mid": v(0, 119.25) * mm, "end": v(-15, 104.25) * mm});
            skLineSegment(sketch, "E84", {"start": v(15, 104.25) * mm, "end": v(15, 92.25) * mm});
            skLineSegment(sketch, "E85", {"start": v(15, 92.25) * mm, "end": v(33, 74.25) * mm});
            skLineSegment(sketch, "E86", {"start": v(-74.25, 0) * mm, "end": v(74.25, 0) * mm, "construction": true});
            skLineSegment(sketch, "E87.MirrorCS", {"start": v(-33, -74.25) * mm, "end": v(-15, -92.25) * mm});
            skLineSegment(sketch, "E88.MirrorCS", {"start": v(-15, -92.25) * mm, "end": v(-15, -104.25) * mm});
            skArc(sketch, "E89.MirrorCS", {"start": v(15, -104.25) * mm, "mid": v(0, -119.25) * mm, "end": v(-15, -104.25) * mm});
            skCircle(sketch, "E90.MirrorC", {"center": v(0, -104.25) * mm, "radius": 6 * mm});
            skLineSegment(sketch, "E91.MirrorCS", {"start": v(15, -104.25) * mm, "end": v(15, -92.25) * mm});
            skLineSegment(sketch, "E92.MirrorCS", {"start": v(15, -92.25) * mm, "end": v(33, -74.25) * mm});
            skSolve(sketch);
        }
        {
            var Q0;
            {var subQ0=sQuery(id+"F16.wireOp",EDGE,"E87.MirrorCS");Q0=makeQuery(id+"F16.imprint","IMPRINT",FACE,{"disambiguationData":[TD([[makeQuery(id+"F16.imprint","IMPRINT",EDGE,{"derivedFrom":subQ0}),1.0]])]});}
            var Q1;
            Q1=makeQuery(id+"F16.imprint","IMPRINT",FACE,{"disambiguationData":[TD([[makeQuery(id+"F16.imprint","IMPRINT",EDGE,{"derivedFrom":makeQuery(id+"F1.opExtrude","CAP_EDGE",EDGE,{"disambiguationData":[OSD([sQuery(id+"F0.wireOp",EDGE,"E1.left")])],"isStart":true})}),-1.0]])]});
            var Q2;
            Q2=makeQuery(id+"F16.imprint","IMPRINT",FACE,{"disambiguationData":[TD([[makeQuery(id+"F16.imprint","IMPRINT",EDGE,{"derivedFrom":sQuery(id+"F16.wireOp",EDGE,"E80")}),-1.0]])]});
            var Q3;
            Q3=makeQuery(id+"F2.opExtrude","CAP_FACE",FACE,{"disambiguationData":[OSD([sQuery(id+"F0.wireOp",EDGE,"E12"),sQuery(id+"F0.wireOp",EDGE,"E13"),sQuery(id+"F0.wireOp",EDGE,"E14"),sQuery(id+"F0.wireOp",EDGE,"E15"),sQuery(id+"F0.wireOp",EDGE,"E17.filletArc"),sQuery(id+"F0.wireOp",EDGE,"E18.filletArc"),sQuery(id+"F0.wireOp",EDGE,"E19.filletArc"),sQuery(id+"F0.wireOp",EDGE,"E20.filletArc"),sQuery(id+"F0.wireOp",EDGE,"E25.0"),sQuery(id+"F0.wireOp",EDGE,"E25.1"),sQuery(id+"F0.wireOp",EDGE,"E25.2"),sQuery(id+"F0.wireOp",EDGE,"E25.3"),sQuery(id+"F0.wireOp",EDGE,"E25.4"),sQuery(id+"F0.wireOp",EDGE,"E25.5"),sQuery(id+"F0.wireOp",EDGE,"E25.6"),sQuery(id+"F0.wireOp",EDGE,"E25.7")])],"isStart":false});
            extrude(context, id + "F17", {"entities" : qUnion([Q0, Q1, Q2]), "operationType" : NewBodyOperationType.ADD, "endBound" : BoundingType.UP_TO_SURFACE, "endBoundEntityFace" : qUnion([Q3]), "depth" : 25 * mm});
        }
    });
